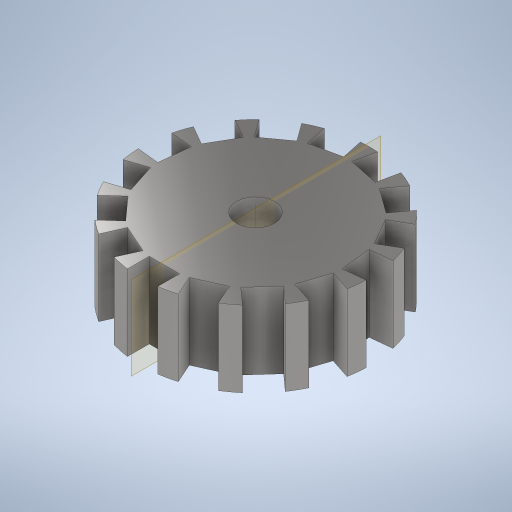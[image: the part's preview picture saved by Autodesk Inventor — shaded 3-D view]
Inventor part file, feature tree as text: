
AUTODESK INVENTOR PART (.ipt)
format: ipt  version: 2023 (Build 270158000, 158)  size: 322,560 bytes
history: native  units: mm
features: sketch x3, extrude x3, plane x1, pattern_circular x1, chamfer x1
ambient origin geometry x8: Origin, YZ Plane, XZ Plane, XY Plane, X Axis, Y Axis, Z Axis, Center Point
bodies: Solid1 (feature_tree)
feature tree (9):
  sketch  "Sketch1"  dims[d0=30.0mm d1=10.0mm d2=10.0mm d3=0.0mm]
  plane  "Work Plane1"
  extrude  "Extrusion1"  Depth=10.0mm TaperAngle=0.0deg
  extrude  "Extrusion2"  Depth=10.0mm
  pattern_circular  "Circular Pattern1"  [2 undecoded]
  extrude  "Extrusion6"  Depth=10.0mm TaperAngle=360.0deg
  chamfer  "Chamfer1"  Distance=5.0mm
  sketch  "Sketch2"  dims[d4=4.0mm d5=10.0mm]
  sketch  "Sketch6"  dims[d6=12.0mm d7=10.0mm d8=0.0mm d9=150.0mm d10=360.0deg d24=5.0mm d25=10.0mm d26=0.0mm d27=1.0mm d28=2.0mm d29=45.0deg]
note: 2 required parameter values undecoded (feature->parameter linkage not recoverable at this tier; creation-order binding heuristic only, values carry confidence <= 0.55)
